# Revit family: Workstations-Multi_Level-Teknion-B_MBH_Overlapping_Bridge_High_Secondary_Desk-R2019
name_source: partatom
category: Furniture
units: mm (PartAtom-declared; Revit-internal decimal feet)

## family parameters
Always vertical = Yes
Cut with Voids When Loaded = No
OmniClass Number = 23.40.20.00
OmniClass Title = General Furniture and Specialties
Room Calculation Point = No
Shared = Yes
Work Plane-Based = No

## types (6) — shared parameters
Assembly Code = E2020200
Manufacturer = Teknion
Manufacturer Fax = 416.661.4586
Part Number = B_MBH
Product Documentation Link = https://www.teknion.com
Product Line = Expansion Casegoods
Product Page URL = https://www.teknion.com
Series = Expansion Casegoods
Sustainability Data = https://www.teknion.com
URL = www.teknion.com
Unit Weight URL = http://www.teknion.com
Warranty = http://www.teknion.com

## per-type parameters (varying)
| type | Depth | Description | Model | Worksurface Thickness |
| 1" Thick WS, 24" Depth | 24 " | Overlapping Bridge – High Secondary Desk, 1" Worksurface Thickness, 24" Depth | BDMBH24___ | 1.016 " |
| 1" Thick WS, 30" Depth | 30 " | Overlapping Bridge – High Secondary Desk, 1" Worksurface Thickness, 30" Depth | BDMBH30___ | 1.016 " |
| 1-3/16" Thick WS, 24" Depth | 24 " | Overlapping Bridge – High Secondary Desk, 1-3/16" Worksurface Thickness, 24" Depth | BMMBH24___ | 1.189 " |
| 1-3/16" Thick WS, 30" Depth | 30 " | Overlapping Bridge – High Secondary Desk, 1-3/16" Worksurface Thickness, 30" Depth | BMMBH30___ | 1.189 " |
| 1-9/16" Thick WS, 30" Depth | 30 " | Overlapping Bridge – High Secondary Desk, 1-9/16" Worksurface Thickness, 30" Depth | BXMBH30___ | 1.555 " |
| 1-9/16" Thick WS, 24" Depth | 24 " | Overlapping Bridge – High Secondary Desk, 1-9/16" Worksurface Thickness, 24" Depth | BXMBH24___ | 1.555 " |

## geometry (parser evidence)
native form markers: Sweep x2
no freeform markers — native parametric forms only
